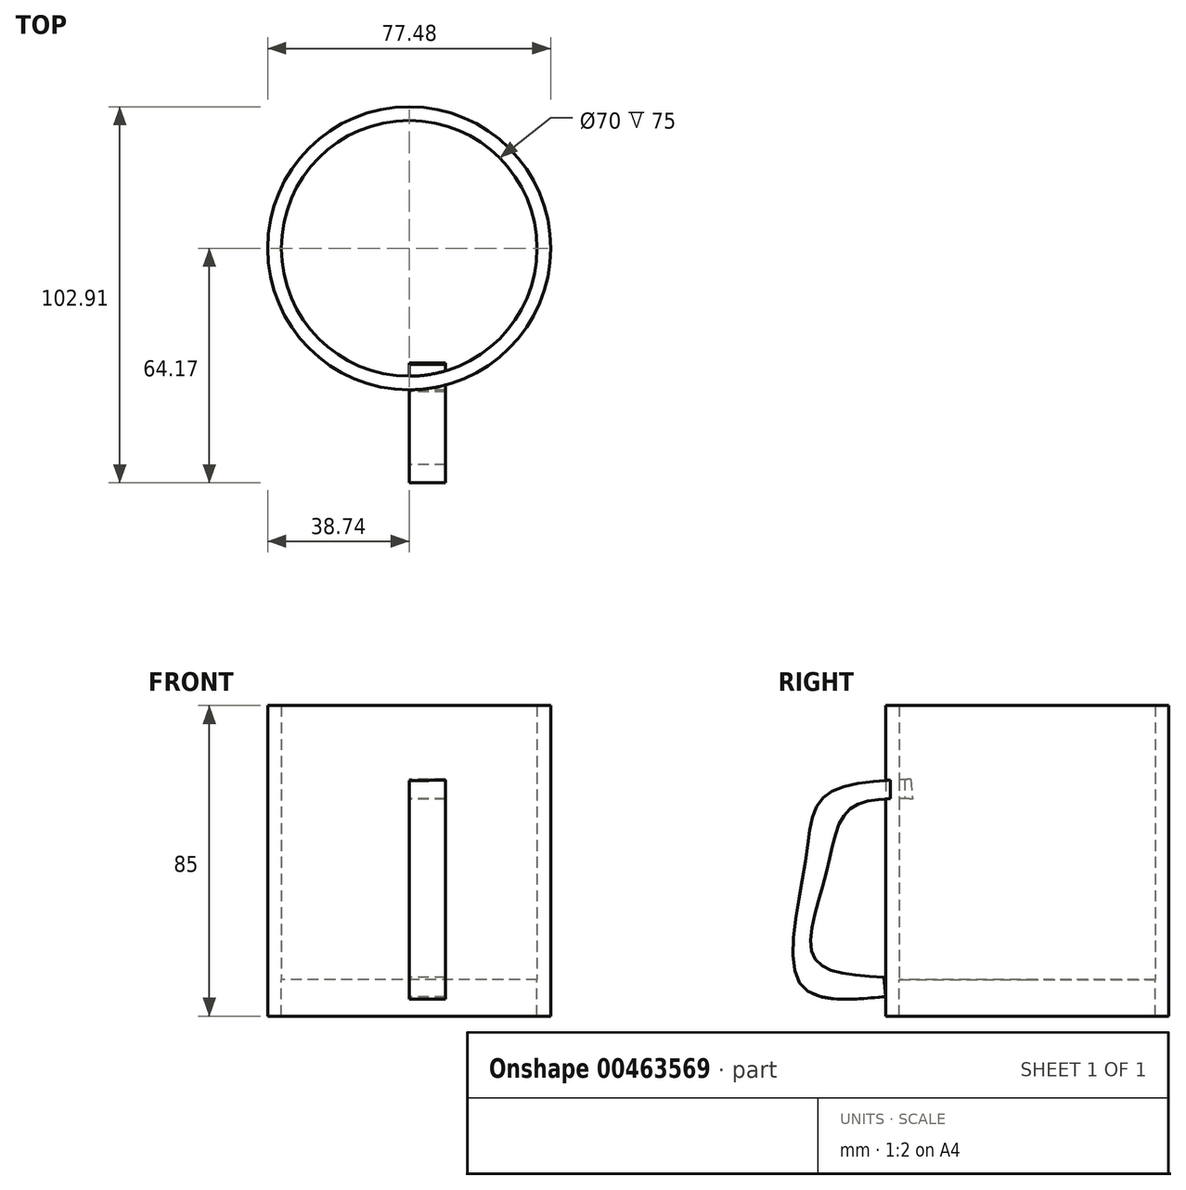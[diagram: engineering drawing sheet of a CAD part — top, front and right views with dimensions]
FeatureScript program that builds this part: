
annotation { "Feature Type Name" : "Feature", "Feature Type Description" : "" }
export const myFeature = defineFeature(function(context is Context, id is Id, definition is map)
    precondition{}
    {
        {
            var Q0;
            Q0=qCreatedBy(makeId("Top.planeOp"),FACE);
            var sketch = newSketch(context, id + "F0", { "sketchPlane" : qUnion([Q0])});
            skCircle(sketch, "E0", {"center": v(0, 0) * mm, "radius": 35 * mm});
            skCircle(sketch, "E1", {"center": v(0, 0) * mm, "radius": 38.74 * mm});
            skSolve(sketch);
        }
        {
            var Q0;
            Q0 = qSketchRegion(id + "F0", true);
            extrude(context, id + "F1", {"entities" : qUnion([Q0]), "depth" : 85 * mm});
        }
        {
            var Q0;
            Q0=qCreatedBy(makeId("Top.planeOp"),FACE);
            var sketch = newSketch(context, id + "F2", { "sketchPlane" : qUnion([Q0])});
            skCircle(sketch, "E2", {"center": v(0, 0) * mm, "radius": 37.82 * mm});
            skSolve(sketch);
        }
        {
            var Q0;
            Q0 = qSketchRegion(id + "F2", true);
            extrude(context, id + "F3", {"entities" : qUnion([Q0]), "operationType" : NewBodyOperationType.ADD, "depth" : 10 * mm});
        }
        {
            var Q0;
            Q0=makeQuery(id+"F3.opExtrude","CAP_FACE",FACE,{"disambiguationData":[OSD([sQuery(id+"F2.wireOp",EDGE,"E2")])],"isStart":false});
            extrude(context, id + "F4", {"entities" : qUnion([Q0]), "oppositeDirection" : true, "depth" : 10 * mm});
        }
        {
            var Q0;
            Q0=qCreatedBy(makeId("Right.planeOp"),FACE);
            var sketch = newSketch(context, id + "F5", { "sketchPlane" : qUnion([Q0])});
            skFitSpline(sketch, "E3", {"points": [v(-31.83, 64.83) * mm, v(-55.45, 60.19) * mm, v(-60.83, 41.81) * mm, v(-62.15, 8.88) * mm, v(-38.78, 5.33) * mm], "startDerivative": vector(-116.13, -4.46) * mm, "endDerivative": vector(120.36, 11.46) * mm});
            skFitSpline(sketch, "E4", {"points": [v(-31.36, 59.43) * mm, v(-48.64, 56.62) * mm, v(-55.05, 39.07) * mm, v(-58.27, 15.95) * mm, v(-39.23, 10.68) * mm], "startDerivative": vector(-86.35, 1.92) * mm, "endDerivative": vector(98.73, -4.72) * mm});
            skLineSegment(sketch, "E5", {"start": v(-31.83, 64.83) * mm, "end": v(-31.36, 59.43) * mm});
            skLineSegment(sketch, "E6", {"start": v(-39.23, 10.68) * mm, "end": v(-38.78, 5.33) * mm});
            skSolve(sketch);
        }
        {
            var Q0;
            Q0 = qSketchRegion(id + "F5", true);
            extrude(context, id + "F6", {"entities" : qUnion([Q0]), "operationType" : NewBodyOperationType.ADD, "depth" : 10 * mm});
        }
    });
